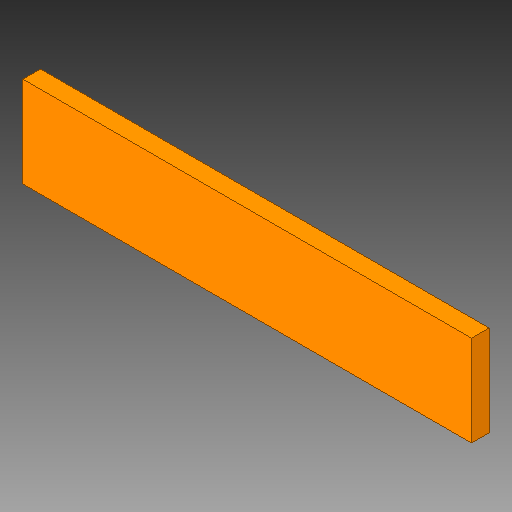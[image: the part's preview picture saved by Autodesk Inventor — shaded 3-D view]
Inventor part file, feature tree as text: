
AUTODESK INVENTOR PART (.ipt)
format: ipt  version: 2018 (Build 220112000, 112)  size: 80,896 bytes
history: native  units: in
note: dims shown in document units (in); Inventor stores cm internally (conversion verified against a paired STEP export)
features: other x1, extrude x1
ambient origin geometry x8: Origin, YZ Plane, XZ Plane, XY Plane, X Axis, Y Axis, Z Axis, Center Point
bodies: Solid1 (feature_tree)
feature tree (2):
  other  "2X10, 2X10_51"
  extrude  "Extrusion1"  Depth=0.0394in TaperAngle=0.0deg
